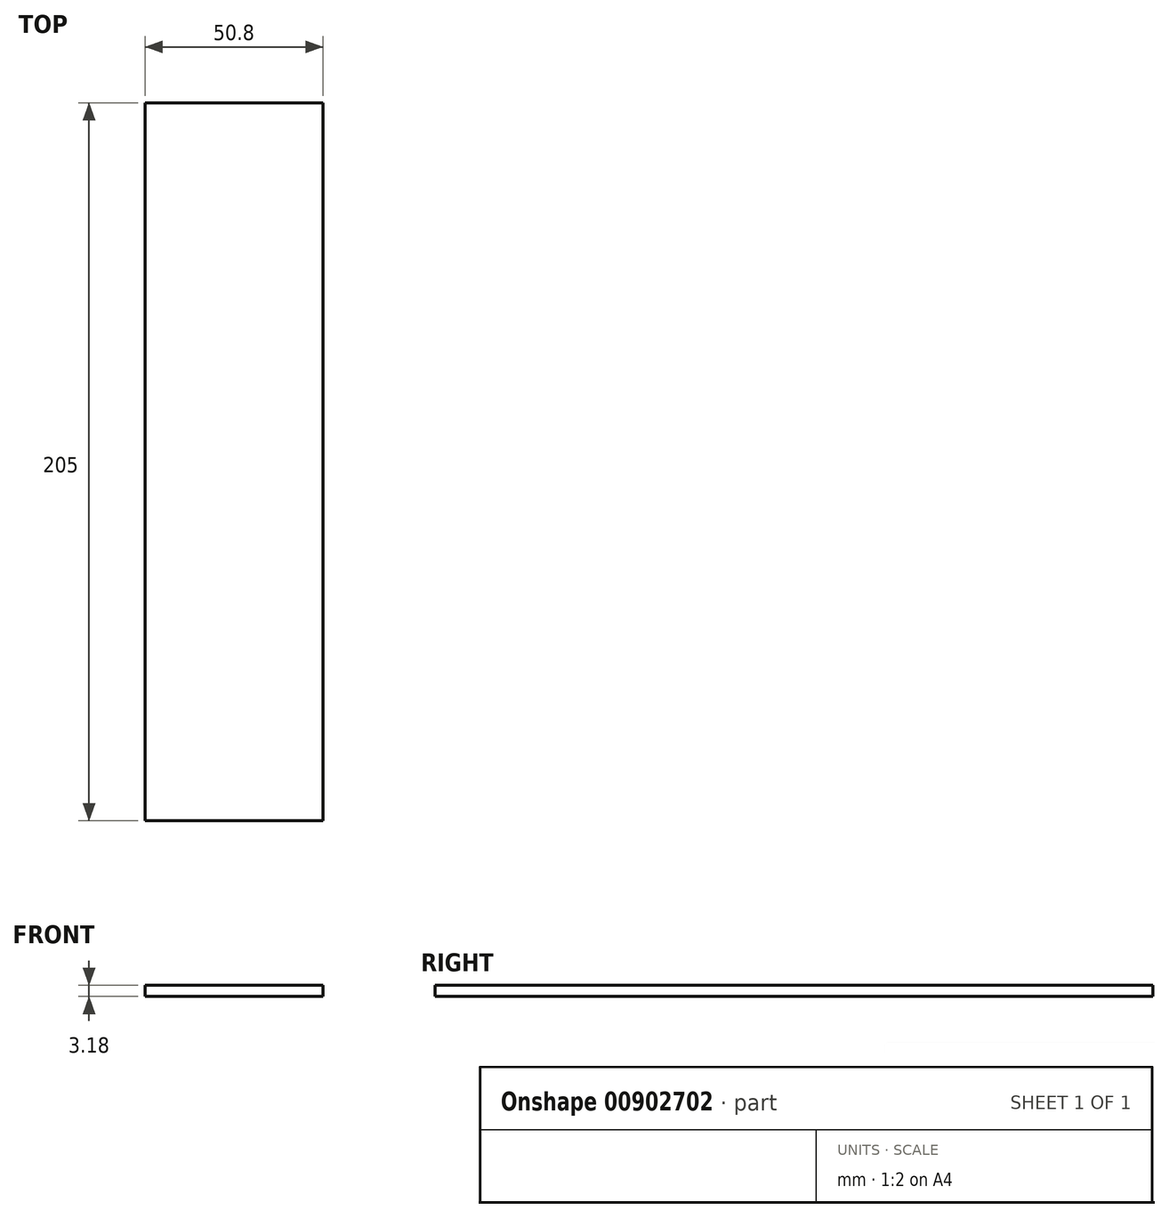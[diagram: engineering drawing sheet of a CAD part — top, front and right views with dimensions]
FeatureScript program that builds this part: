
annotation { "Feature Type Name" : "Feature", "Feature Type Description" : "" }
export const myFeature = defineFeature(function(context is Context, id is Id, definition is map)
    precondition{}
    {
        {
            var Q0;
            Q0=qCreatedBy(makeId("Front.planeOp"),FACE);
            var sketch = newSketch(context, id + "F0", { "sketchPlane" : qUnion([Q0])});
            skLineSegment(sketch, "E0.bottom", {"start": v(25.4, 1.59) * mm, "end": v(-25.4, 1.59) * mm});
            skLineSegment(sketch, "E0.top", {"start": v(25.4, -1.59) * mm, "end": v(-25.4, -1.59) * mm});
            skLineSegment(sketch, "E0.left", {"start": v(25.4, 1.59) * mm, "end": v(25.4, -1.59) * mm});
            skLineSegment(sketch, "E0.right", {"start": v(-25.4, 1.59) * mm, "end": v(-25.4, -1.59) * mm});
            skPoint(sketch, "E0.middle", {"position": v(0, 0) * mm});
            skSolve(sketch);
        }
        {
            var Q0;
            Q0 = qSketchRegion(id + "F0", true);
            extrude(context, id + "F1", {"entities" : qUnion([Q0]), "depth" : 205 * mm, "offsetDistance" : 25 * mm});
        }
    });
